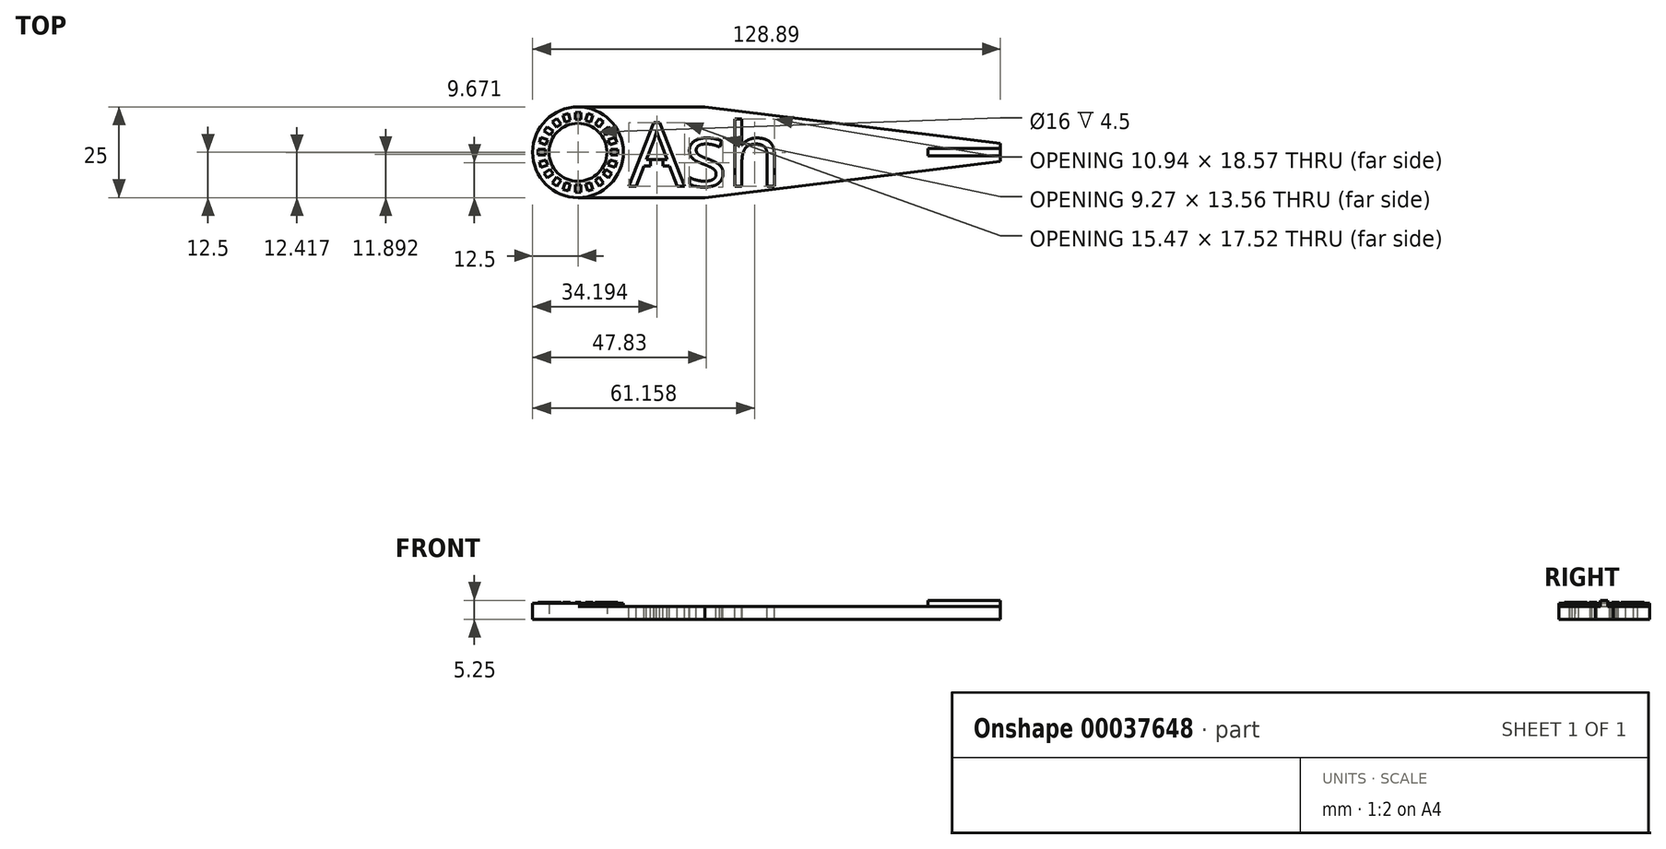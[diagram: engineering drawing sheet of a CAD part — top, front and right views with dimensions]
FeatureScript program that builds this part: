
annotation { "Feature Type Name" : "Feature", "Feature Type Description" : "" }
export const myFeature = defineFeature(function(context is Context, id is Id, definition is map)
    precondition{}
    {
        {
            var Q0;
            Q0=qCreatedBy(makeId("Top.planeOp"),FACE);
            var sketch = newSketch(context, id + "F0", { "sketchPlane" : qUnion([Q0])});
            skCircle(sketch, "E0", {"center": v(0, 0) * mm, "radius": 8 * mm});
            skCircle(sketch, "E1", {"center": v(0, 0) * mm, "radius": 12.5 * mm});
            skLineSegment(sketch, "E2", {"start": v(0, 12.5) * mm, "end": v(35, 12.5) * mm});
            skPoint(sketch, "E3", {"position": v(0, 12.5) * mm});
            skLineSegment(sketch, "E4", {"start": v(0, 0) * mm, "end": v(34.78, 0) * mm, "construction": true});
            skLineSegment(sketch, "E5.MirrorCS", {"start": v(0, -12.5) * mm, "end": v(35, -12.5) * mm});
            skLineSegment(sketch, "E6", {"start": v(35, 12.5) * mm, "end": v(96.85, 12.5) * mm, "construction": true});
            skLineSegment(sketch, "E7", {"start": v(35, 12.5) * mm, "end": v(116.39, 2.5) * mm});
            skLineSegment(sketch, "E8.MirrorCS", {"start": v(35, -12.5) * mm, "end": v(116.39, -2.5) * mm});
            skLineSegment(sketch, "E9", {"start": v(116.39, 2.5) * mm, "end": v(116.39, -2.5) * mm});
            skSolve(sketch);
        }
        {
            var Q0;
            Q0 = qSketchRegion(id + "F0", true);
            extrude(context, id + "F1", {"entities" : qUnion([Q0]), "depth" : 3.5 * mm});
        }
        {
            var Q0;
            Q0=makeQuery(id+"F1.opExtrude","CAP_FACE",FACE,{"disambiguationData":[OSD([sQuery(id+"F0.wireOp",EDGE,"E0"),sQuery(id+"F0.wireOp",EDGE,"E1"),sQuery(id+"F0.wireOp",EDGE,"E2"),sQuery(id+"F0.wireOp",EDGE,"E5.MirrorCS"),sQuery(id+"F0.wireOp",EDGE,"E7"),sQuery(id+"F0.wireOp",EDGE,"E8.MirrorCS"),sQuery(id+"F0.wireOp",EDGE,"E9")])],"isStart":false});
            var sketch = newSketch(context, id + "F2", { "sketchPlane" : qUnion([Q0])});
            skCircle(sketch, "E10", {"center": v(0, 0) * mm, "radius": 12.5 * mm});
            skCircle(sketch, "E11", {"center": v(0, 0) * mm, "radius": 8 * mm});
            skSolve(sketch);
        }
        {
            var Q0;
            Q0 = qSketchRegion(id + "F2", true);
            extrude(context, id + "F3", {"entities" : qUnion([Q0]), "operationType" : NewBodyOperationType.ADD, "depth" : 1 * mm});
        }
        {
            var Q0;
            Q0=makeQuery(id+"F3.opExtrude","CAP_FACE",FACE,{"disambiguationData":[OSD([sQuery(id+"F2.wireOp",EDGE,"E10"),sQuery(id+"F2.wireOp",EDGE,"E11")])],"isStart":false});
            var sketch = newSketch(context, id + "F4", { "sketchPlane" : qUnion([Q0])});
            skLineSegment(sketch, "E12.bottom", {"start": v(-0.75, 11) * mm, "end": v(0.75, 11) * mm});
            skLineSegment(sketch, "E12.top", {"start": v(-0.75, 9) * mm, "end": v(0.75, 9) * mm});
            skLineSegment(sketch, "E12.left", {"start": v(-0.75, 11) * mm, "end": v(-0.75, 9) * mm});
            skLineSegment(sketch, "E12.right", {"start": v(0.75, 11) * mm, "end": v(0.75, 9) * mm});
            skPoint(sketch, "E13", {"position": v(0, 8) * mm});
            skLineSegment(sketch, "E14.1.0", {"start": v(-4.11, 10.23) * mm, "end": v(-2.69, 10.7) * mm});
            skLineSegment(sketch, "E14.1.1", {"start": v(-4.11, 10.23) * mm, "end": v(-3.5, 8.33) * mm});
            skLineSegment(sketch, "E14.1.2", {"start": v(-3.5, 8.33) * mm, "end": v(-2.07, 8.8) * mm});
            skLineSegment(sketch, "E14.1.3", {"start": v(-2.69, 10.7) * mm, "end": v(-2.07, 8.8) * mm});
            skLineSegment(sketch, "E14.2.0", {"start": v(-7.07, 8.46) * mm, "end": v(-5.86, 9.34) * mm});
            skLineSegment(sketch, "E14.2.1", {"start": v(-7.07, 8.46) * mm, "end": v(-5.9, 6.84) * mm});
            skLineSegment(sketch, "E14.2.2", {"start": v(-5.9, 6.84) * mm, "end": v(-4.68, 7.72) * mm});
            skLineSegment(sketch, "E14.2.3", {"start": v(-5.86, 9.34) * mm, "end": v(-4.68, 7.72) * mm});
            skLineSegment(sketch, "E14.3.0", {"start": v(-9.34, 5.86) * mm, "end": v(-8.46, 7.07) * mm});
            skLineSegment(sketch, "E14.3.1", {"start": v(-9.34, 5.86) * mm, "end": v(-7.72, 4.68) * mm});
            skLineSegment(sketch, "E14.3.2", {"start": v(-7.72, 4.68) * mm, "end": v(-6.84, 5.9) * mm});
            skLineSegment(sketch, "E14.3.3", {"start": v(-8.46, 7.07) * mm, "end": v(-6.84, 5.9) * mm});
            skLineSegment(sketch, "E14.4.0", {"start": v(-10.7, 2.69) * mm, "end": v(-10.23, 4.11) * mm});
            skLineSegment(sketch, "E14.4.1", {"start": v(-10.7, 2.69) * mm, "end": v(-8.8, 2.07) * mm});
            skLineSegment(sketch, "E14.4.2", {"start": v(-8.8, 2.07) * mm, "end": v(-8.33, 3.5) * mm});
            skLineSegment(sketch, "E14.4.3", {"start": v(-10.23, 4.11) * mm, "end": v(-8.33, 3.5) * mm});
            skLineSegment(sketch, "E14.5.0", {"start": v(-11, -0.75) * mm, "end": v(-11, 0.75) * mm});
            skLineSegment(sketch, "E14.5.1", {"start": v(-11, -0.75) * mm, "end": v(-9, -0.75) * mm});
            skLineSegment(sketch, "E14.5.2", {"start": v(-9, -0.75) * mm, "end": v(-9, 0.75) * mm});
            skLineSegment(sketch, "E14.5.3", {"start": v(-11, 0.75) * mm, "end": v(-9, 0.75) * mm});
            skLineSegment(sketch, "E14.6.0", {"start": v(-10.23, -4.11) * mm, "end": v(-10.7, -2.69) * mm});
            skLineSegment(sketch, "E14.6.1", {"start": v(-10.23, -4.11) * mm, "end": v(-8.33, -3.5) * mm});
            skLineSegment(sketch, "E14.6.2", {"start": v(-8.33, -3.5) * mm, "end": v(-8.8, -2.07) * mm});
            skLineSegment(sketch, "E14.6.3", {"start": v(-10.7, -2.69) * mm, "end": v(-8.8, -2.07) * mm});
            skLineSegment(sketch, "E14.7.0", {"start": v(-8.46, -7.07) * mm, "end": v(-9.34, -5.86) * mm});
            skLineSegment(sketch, "E14.7.1", {"start": v(-8.46, -7.07) * mm, "end": v(-6.84, -5.9) * mm});
            skLineSegment(sketch, "E14.7.2", {"start": v(-6.84, -5.9) * mm, "end": v(-7.72, -4.68) * mm});
            skLineSegment(sketch, "E14.7.3", {"start": v(-9.34, -5.86) * mm, "end": v(-7.72, -4.68) * mm});
            skLineSegment(sketch, "E14.8.0", {"start": v(-5.86, -9.34) * mm, "end": v(-7.07, -8.46) * mm});
            skLineSegment(sketch, "E14.8.1", {"start": v(-5.86, -9.34) * mm, "end": v(-4.68, -7.72) * mm});
            skLineSegment(sketch, "E14.8.2", {"start": v(-4.68, -7.72) * mm, "end": v(-5.9, -6.84) * mm});
            skLineSegment(sketch, "E14.8.3", {"start": v(-7.07, -8.46) * mm, "end": v(-5.9, -6.84) * mm});
            skLineSegment(sketch, "E14.9.0", {"start": v(-2.69, -10.7) * mm, "end": v(-4.11, -10.23) * mm});
            skLineSegment(sketch, "E14.9.1", {"start": v(-2.69, -10.7) * mm, "end": v(-2.07, -8.8) * mm});
            skLineSegment(sketch, "E14.9.2", {"start": v(-2.07, -8.8) * mm, "end": v(-3.5, -8.33) * mm});
            skLineSegment(sketch, "E14.9.3", {"start": v(-4.11, -10.23) * mm, "end": v(-3.5, -8.33) * mm});
            skLineSegment(sketch, "E14.10.0", {"start": v(0.75, -11) * mm, "end": v(-0.75, -11) * mm});
            skLineSegment(sketch, "E14.10.1", {"start": v(0.75, -11) * mm, "end": v(0.75, -9) * mm});
            skLineSegment(sketch, "E14.10.2", {"start": v(0.75, -9) * mm, "end": v(-0.75, -9) * mm});
            skLineSegment(sketch, "E14.10.3", {"start": v(-0.75, -11) * mm, "end": v(-0.75, -9) * mm});
            skLineSegment(sketch, "E14.11.0", {"start": v(4.11, -10.23) * mm, "end": v(2.69, -10.7) * mm});
            skLineSegment(sketch, "E14.11.1", {"start": v(4.11, -10.23) * mm, "end": v(3.5, -8.33) * mm});
            skLineSegment(sketch, "E14.11.2", {"start": v(3.5, -8.33) * mm, "end": v(2.07, -8.8) * mm});
            skLineSegment(sketch, "E14.11.3", {"start": v(2.69, -10.7) * mm, "end": v(2.07, -8.8) * mm});
            skLineSegment(sketch, "E14.12.0", {"start": v(7.07, -8.46) * mm, "end": v(5.86, -9.34) * mm});
            skLineSegment(sketch, "E14.12.1", {"start": v(7.07, -8.46) * mm, "end": v(5.9, -6.84) * mm});
            skLineSegment(sketch, "E14.12.2", {"start": v(5.9, -6.84) * mm, "end": v(4.68, -7.72) * mm});
            skLineSegment(sketch, "E14.12.3", {"start": v(5.86, -9.34) * mm, "end": v(4.68, -7.72) * mm});
            skLineSegment(sketch, "E14.13.0", {"start": v(9.34, -5.86) * mm, "end": v(8.46, -7.07) * mm});
            skLineSegment(sketch, "E14.13.1", {"start": v(9.34, -5.86) * mm, "end": v(7.72, -4.68) * mm});
            skLineSegment(sketch, "E14.13.2", {"start": v(7.72, -4.68) * mm, "end": v(6.84, -5.9) * mm});
            skLineSegment(sketch, "E14.13.3", {"start": v(8.46, -7.07) * mm, "end": v(6.84, -5.9) * mm});
            skLineSegment(sketch, "E14.14.0", {"start": v(10.7, -2.69) * mm, "end": v(10.23, -4.11) * mm});
            skLineSegment(sketch, "E14.14.1", {"start": v(10.7, -2.69) * mm, "end": v(8.8, -2.07) * mm});
            skLineSegment(sketch, "E14.14.2", {"start": v(8.8, -2.07) * mm, "end": v(8.33, -3.5) * mm});
            skLineSegment(sketch, "E14.14.3", {"start": v(10.23, -4.11) * mm, "end": v(8.33, -3.5) * mm});
            skLineSegment(sketch, "E14.15.0", {"start": v(11, 0.75) * mm, "end": v(11, -0.75) * mm});
            skLineSegment(sketch, "E14.15.1", {"start": v(11, 0.75) * mm, "end": v(9, 0.75) * mm});
            skLineSegment(sketch, "E14.15.2", {"start": v(9, 0.75) * mm, "end": v(9, -0.75) * mm});
            skLineSegment(sketch, "E14.15.3", {"start": v(11, -0.75) * mm, "end": v(9, -0.75) * mm});
            skLineSegment(sketch, "E14.16.0", {"start": v(10.23, 4.11) * mm, "end": v(10.7, 2.69) * mm});
            skLineSegment(sketch, "E14.16.1", {"start": v(10.23, 4.11) * mm, "end": v(8.33, 3.5) * mm});
            skLineSegment(sketch, "E14.16.2", {"start": v(8.33, 3.5) * mm, "end": v(8.8, 2.07) * mm});
            skLineSegment(sketch, "E14.16.3", {"start": v(10.7, 2.69) * mm, "end": v(8.8, 2.07) * mm});
            skLineSegment(sketch, "E14.17.0", {"start": v(8.46, 7.07) * mm, "end": v(9.34, 5.86) * mm});
            skLineSegment(sketch, "E14.17.1", {"start": v(8.46, 7.07) * mm, "end": v(6.84, 5.9) * mm});
            skLineSegment(sketch, "E14.17.2", {"start": v(6.84, 5.9) * mm, "end": v(7.72, 4.68) * mm});
            skLineSegment(sketch, "E14.17.3", {"start": v(9.34, 5.86) * mm, "end": v(7.72, 4.68) * mm});
            skLineSegment(sketch, "E14.18.0", {"start": v(5.86, 9.34) * mm, "end": v(7.07, 8.46) * mm});
            skLineSegment(sketch, "E14.18.1", {"start": v(5.86, 9.34) * mm, "end": v(4.68, 7.72) * mm});
            skLineSegment(sketch, "E14.18.2", {"start": v(4.68, 7.72) * mm, "end": v(5.9, 6.84) * mm});
            skLineSegment(sketch, "E14.18.3", {"start": v(7.07, 8.46) * mm, "end": v(5.9, 6.84) * mm});
            skLineSegment(sketch, "E14.19.0", {"start": v(2.69, 10.7) * mm, "end": v(4.11, 10.23) * mm});
            skLineSegment(sketch, "E14.19.1", {"start": v(2.69, 10.7) * mm, "end": v(2.07, 8.8) * mm});
            skLineSegment(sketch, "E14.19.2", {"start": v(2.07, 8.8) * mm, "end": v(3.5, 8.33) * mm});
            skLineSegment(sketch, "E14.19.3", {"start": v(4.11, 10.23) * mm, "end": v(3.5, 8.33) * mm});
            skPoint(sketch, "E14.center", {"position": v(0, 0) * mm});
            skSolve(sketch);
        }
        {
            var Q0;
            Q0 = qSketchRegion(id + "F4", true);
            extrude(context, id + "F5", {"entities" : qUnion([Q0]), "operationType" : NewBodyOperationType.ADD, "depth" : .25 * mm});
        }
        {
            var Q0;
            Q0=makeQuery(id+"F1.opExtrude","CAP_FACE",FACE,{"disambiguationData":[OSD([sQuery(id+"F0.wireOp",EDGE,"E0"),sQuery(id+"F0.wireOp",EDGE,"E1"),sQuery(id+"F0.wireOp",EDGE,"E2"),sQuery(id+"F0.wireOp",EDGE,"E5.MirrorCS"),sQuery(id+"F0.wireOp",EDGE,"E7"),sQuery(id+"F0.wireOp",EDGE,"E8.MirrorCS"),sQuery(id+"F0.wireOp",EDGE,"E9")])],"isStart":false});
            var sketch = newSketch(context, id + "F6", { "sketchPlane" : qUnion([Q0])});
            skLineSegment(sketch, "E15.bottom", {"start": v(116.39, 1) * mm, "end": v(96.39, 1) * mm});
            skLineSegment(sketch, "E15.top", {"start": v(116.39, -1) * mm, "end": v(96.39, -1) * mm});
            skLineSegment(sketch, "E15.left", {"start": v(116.39, 1) * mm, "end": v(116.39, -1) * mm});
            skLineSegment(sketch, "E15.right", {"start": v(96.39, 1) * mm, "end": v(96.39, -1) * mm});
            skSolve(sketch);
        }
        {
            var Q0;
            Q0 = qSketchRegion(id + "F6", true);
            extrude(context, id + "F7", {"entities" : qUnion([Q0]), "operationType" : NewBodyOperationType.ADD, "depth" : 1.75 * mm});
        }
        {
            var Q0;
            Q0=makeQuery(id+"F1.opExtrude","CAP_FACE",FACE,{"disambiguationData":[OSD([sQuery(id+"F0.wireOp",EDGE,"E0"),sQuery(id+"F0.wireOp",EDGE,"E1"),sQuery(id+"F0.wireOp",EDGE,"E2"),sQuery(id+"F0.wireOp",EDGE,"E5.MirrorCS"),sQuery(id+"F0.wireOp",EDGE,"E7"),sQuery(id+"F0.wireOp",EDGE,"E8.MirrorCS"),sQuery(id+"F0.wireOp",EDGE,"E9")])],"isStart":false});
            var sketch = newSketch(context, id + "F8", { "sketchPlane" : qUnion([Q0])});
            skText(sketch, "E16", { "text": "Ash", "fontName": "OpenSans-Regular.ttf"});
            const initialGuessF8  = {"E16": [0.01396, -0.00937, 1, 0, 0.0176]};
            skSetInitialGuess(sketch, initialGuessF8);
            skSolve(sketch);
        }
        {
            var Q0;
            Q0 = qSketchRegion(id + "F8", true);
            extrude(context, id + "F9", {"entities" : qUnion([Q0]), "operationType" : NewBodyOperationType.REMOVE, "endBound" : BoundingType.SYMMETRIC, "oppositeDirection" : true, "depth" : 50 * mm});
        }
        {
            var Q0;
            Q0=makeQuery(id+"F9.boolean.opBoolean","SPLIT",FACE,{"disambiguationData":[TD([makeQuery(id+"F9.opExtrude","SWEPT_FACE",FACE,{"disambiguationData":[OSD([sQuery(id+"F8.wireOp",EDGE,"E16.sketch_text.stroke-8")])]})])],"derivedFrom":makeQuery(id+"F1.opExtrude","CAP_FACE",FACE,{"disambiguationData":[OSD([sQuery(id+"F0.wireOp",EDGE,"E0"),sQuery(id+"F0.wireOp",EDGE,"E1"),sQuery(id+"F0.wireOp",EDGE,"E2"),sQuery(id+"F0.wireOp",EDGE,"E5.MirrorCS"),sQuery(id+"F0.wireOp",EDGE,"E7"),sQuery(id+"F0.wireOp",EDGE,"E8.MirrorCS"),sQuery(id+"F0.wireOp",EDGE,"E9")])],"isStart":false})});
            var sketch = newSketch(context, id + "F10", { "sketchPlane" : qUnion([Q0])});
            skLineSegment(sketch, "E17.bottom", {"start": v(19.95, -2) * mm, "end": v(23.45, -2) * mm});
            skLineSegment(sketch, "E17.top", {"start": v(19.95, -3.82) * mm, "end": v(23.45, -3.82) * mm});
            skLineSegment(sketch, "E17.left", {"start": v(19.95, -2) * mm, "end": v(19.95, -3.82) * mm});
            skLineSegment(sketch, "E17.right", {"start": v(23.45, -2) * mm, "end": v(23.45, -3.82) * mm});
            skSolve(sketch);
        }
        {
            var Q0;
            Q0 = qSketchRegion(id + "F10", true);
            extrude(context, id + "F11", {"entities" : qUnion([Q0]), "operationType" : NewBodyOperationType.ADD, "oppositeDirection" : true, "depth" : 3.5 * mm});
        }
    });
